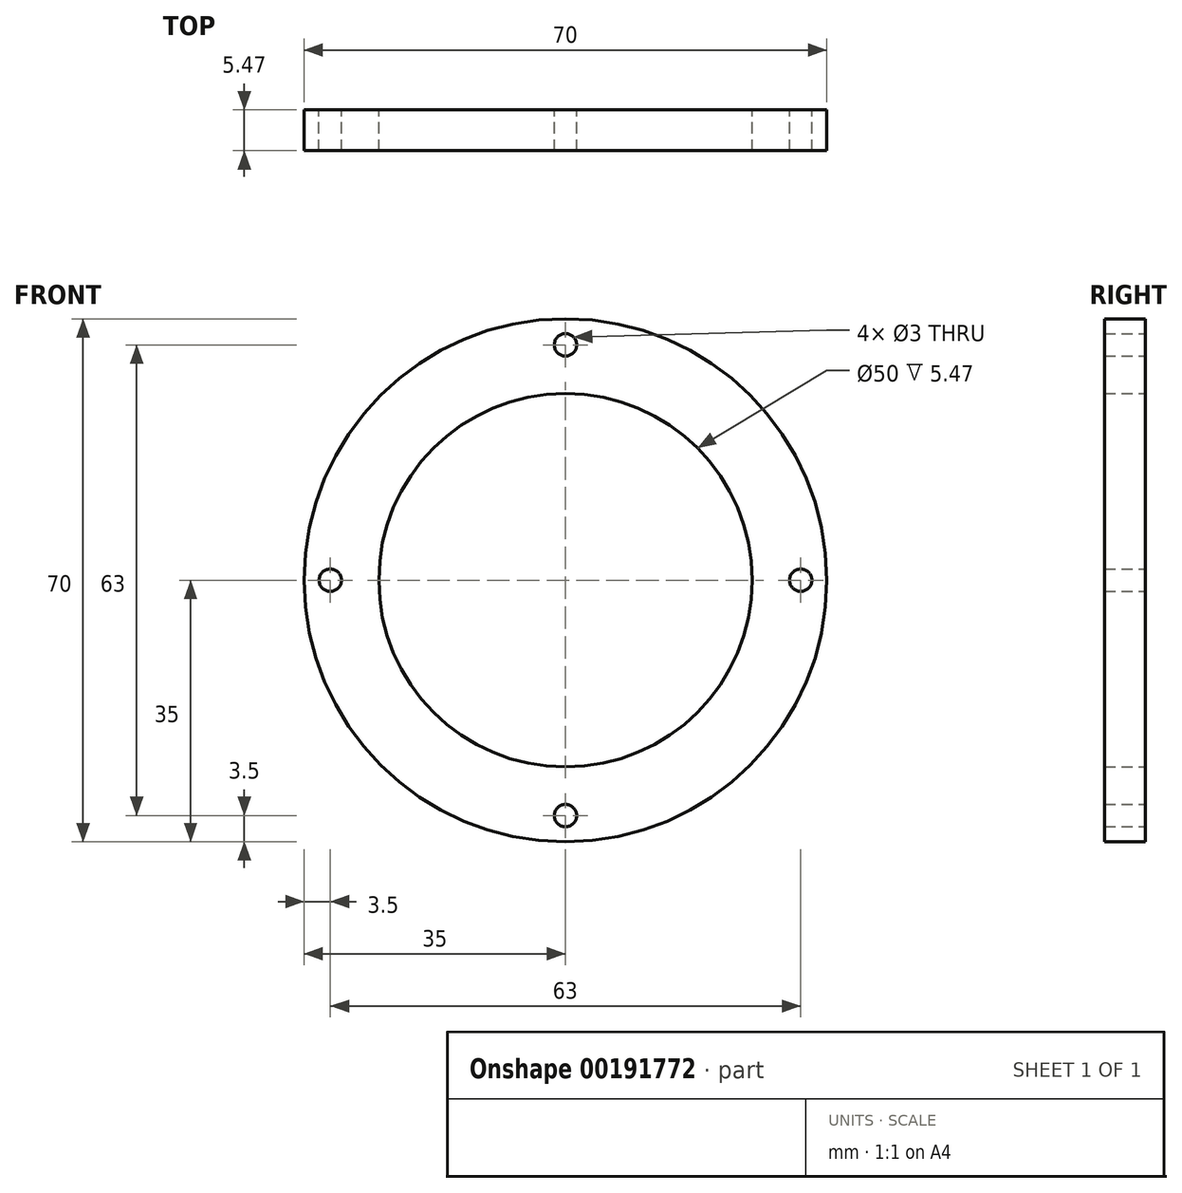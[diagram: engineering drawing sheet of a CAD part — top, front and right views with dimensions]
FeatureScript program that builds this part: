
annotation { "Feature Type Name" : "Feature", "Feature Type Description" : "" }
export const myFeature = defineFeature(function(context is Context, id is Id, definition is map)
    precondition{}
    {
        {
            var Q0;
            Q0=qCreatedBy(makeId("Front.planeOp"),FACE);
            var sketch = newSketch(context, id + "F0", { "sketchPlane" : qUnion([Q0])});
            skCircle(sketch, "E0", {"center": v(0, 0) * mm, "radius": 25 * mm});
            skCircle(sketch, "E1", {"center": v(0, 0) * mm, "radius": 35 * mm});
            skCircle(sketch, "E2", {"center": v(0, 0) * mm, "radius": 31.5 * mm, "construction": true});
            skCircle(sketch, "E3", {"center": v(0, 31.5) * mm, "radius": 1.5 * mm});
            skCircle(sketch, "E4.1.0", {"center": v(-31.5, 0) * mm, "radius": 1.5 * mm});
            skCircle(sketch, "E4.2.0", {"center": v(0, -31.5) * mm, "radius": 1.5 * mm});
            skCircle(sketch, "E4.3.0", {"center": v(31.5, 0) * mm, "radius": 1.5 * mm});
            skSolve(sketch);
        }
        {
            var Q0;
            Q0=makeQuery(id+"F0.imprint","IMPRINT",FACE,{"disambiguationData":[TD([[makeQuery(id+"F0.imprint","IMPRINT",EDGE,{"derivedFrom":sQuery(id+"F0.wireOp",EDGE,"E0")}),-1.0]])]});
            extrude(context, id + "F1", {"entities" : qUnion([Q0]), "depth" : 5.47 * mm});
        }
    });
